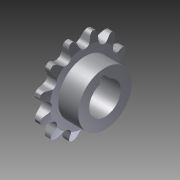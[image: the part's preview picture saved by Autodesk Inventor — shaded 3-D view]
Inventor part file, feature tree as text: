
AUTODESK INVENTOR PART (.ipt)
format: ipt  version: 2012 (Build 160160000, 160)  size: 371,200 bytes
history: native  units: in
note: dims shown in document units (in); Inventor stores cm internally (conversion verified against a paired STEP export)
features: sketch x2, extrude x2, revolve x1
ambient origin geometry x8: Origin, YZ Plane, XZ Plane, XY Plane, X Axis, Y Axis, Z Axis, Center Point
bodies: Solid1 (feature_tree)
feature tree (5):
  revolve  "Revolution1"  [1 undecoded]
  sketch  "Sketch3"  dims[d3=0.55in d4=0.3346in d5=90.0deg d12=0.25in d26=30.0deg d27=0.0649in d29=4.7244in d30=0.0684in d31=0.483in d32=0.0469in d33=0.0684in d34=0.125in d35=360.0deg d36=0.25in d37=0.55in d38=1.1in d39=1.0in d40=0.0in d41=0.125in d42=0.125in d43=0.0625in d44=0.3937in d45=0.2594in d46=1.0in d47=0.0in]
  extrude  "Extrusion2"  Depth=0.3346in
  extrude  "Extrusion3"  TaperAngle=90.0deg  [1 undecoded]
  sketch  "Sketch1"  dims[d0=0.125in d1=0.1969in]
note: 2 required parameter values undecoded (feature->parameter linkage not recoverable at this tier; creation-order binding heuristic only, values carry confidence <= 0.55)